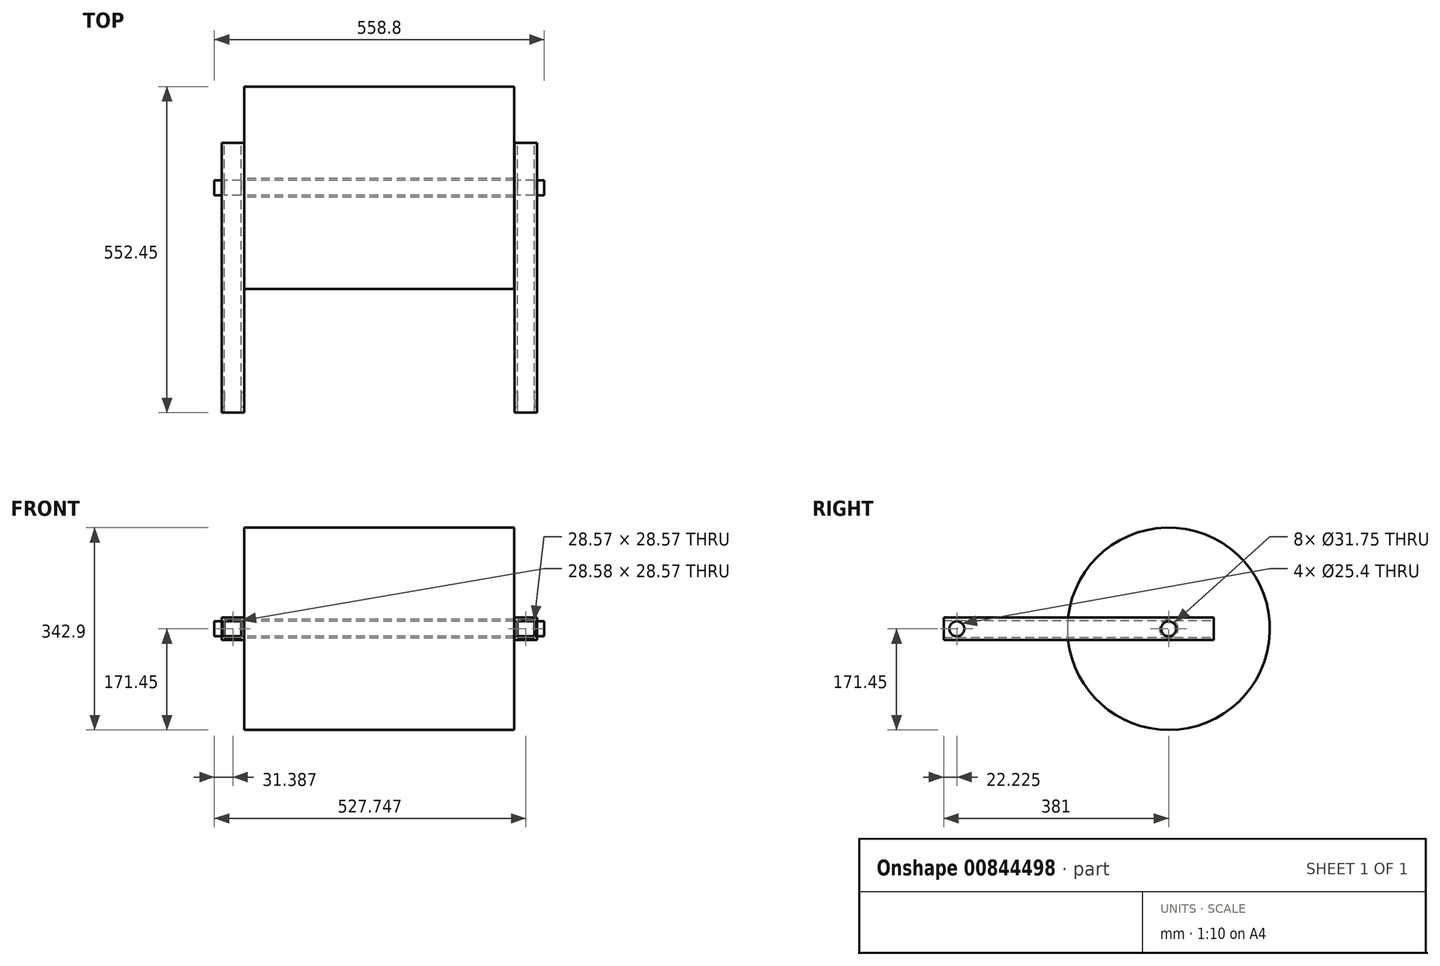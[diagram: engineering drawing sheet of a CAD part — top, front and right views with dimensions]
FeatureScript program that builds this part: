
annotation { "Feature Type Name" : "Feature", "Feature Type Description" : "" }
export const myFeature = defineFeature(function(context is Context, id is Id, definition is map)
    precondition{}
    {
        {
            var Q0;
            Q0=qCreatedBy(makeId("Right.planeOp"),FACE);
            var sketch = newSketch(context, id + "F0", { "sketchPlane" : qUnion([Q0])});
            skCircle(sketch, "E0", {"center": v(0, 0) * mm, "radius": 171.45 * mm});
            skCircle(sketch, "E1", {"center": v(0, 0) * mm, "radius": 15.88 * mm});
            skSolve(sketch);
        }
        {
            var Q0;
            Q0 = qSketchRegion(id + "F0", true);
            extrude(context, id + "F1", {"entities" : qUnion([Q0]), "depth" : 457.2 * mm, "offsetDistance" : 25.4 * mm, "symmetric" : true});
        }
        {
            var Q0;
            Q0=qCreatedBy(makeId("Right.planeOp"),FACE);
            var sketch = newSketch(context, id + "F2", { "sketchPlane" : qUnion([Q0])});
            skCircle(sketch, "E2", {"center": v(0, 0) * mm, "radius": 12.7 * mm});
            skSolve(sketch);
        }
        {
            var Q0;
            Q0 = qSketchRegion(id + "F2", true);
            extrude(context, id + "F3", {"entities" : qUnion([Q0]), "depth" : 558.8 * mm, "offsetDistance" : 25.4 * mm, "symmetric" : true});
        }
        {
            var Q0;
            Q0=qCreatedBy(makeId("Front.planeOp"),FACE);
            var sketch = newSketch(context, id + "F4", { "sketchPlane" : qUnion([Q0])});
            skLineSegment(sketch, "E3.bottom", {"start": v(267.4, -19.05) * mm, "end": v(229.3, -19.05) * mm});
            skLineSegment(sketch, "E3.top", {"start": v(267.4, 19.05) * mm, "end": v(229.3, 19.05) * mm});
            skLineSegment(sketch, "E3.left", {"start": v(267.4, -19.05) * mm, "end": v(267.4, 19.05) * mm});
            skLineSegment(sketch, "E3.right", {"start": v(229.3, -19.05) * mm, "end": v(229.3, 19.05) * mm});
            skPoint(sketch, "E3.middle", {"position": v(248.35, 0) * mm});
            skLineSegment(sketch, "E4.bottom", {"start": v(-228.96, -19.05) * mm, "end": v(-267.06, -19.05) * mm});
            skLineSegment(sketch, "E4.top", {"start": v(-228.96, 19.05) * mm, "end": v(-267.06, 19.05) * mm});
            skLineSegment(sketch, "E4.left", {"start": v(-228.96, -19.05) * mm, "end": v(-228.96, 19.05) * mm});
            skLineSegment(sketch, "E4.right", {"start": v(-267.06, -19.05) * mm, "end": v(-267.06, 19.05) * mm});
            skPoint(sketch, "E4.middle", {"position": v(-248.01, 0) * mm});
            skLineSegment(sketch, "E5.0", {"start": v(262.63, 14.29) * mm, "end": v(234.06, 14.29) * mm});
            skLineSegment(sketch, "E5.1", {"start": v(262.63, -14.29) * mm, "end": v(262.63, 14.29) * mm});
            skLineSegment(sketch, "E5.2", {"start": v(262.63, -14.29) * mm, "end": v(234.06, -14.29) * mm});
            skLineSegment(sketch, "E5.3", {"start": v(234.06, -14.29) * mm, "end": v(234.06, 14.29) * mm});
            skLineSegment(sketch, "E6.0", {"start": v(-233.73, -14.29) * mm, "end": v(-262.3, -14.29) * mm});
            skLineSegment(sketch, "E6.1", {"start": v(-233.73, -14.29) * mm, "end": v(-233.73, 14.29) * mm});
            skLineSegment(sketch, "E6.2", {"start": v(-233.73, 14.29) * mm, "end": v(-262.3, 14.29) * mm});
            skLineSegment(sketch, "E6.3", {"start": v(-262.3, -14.29) * mm, "end": v(-262.3, 14.29) * mm});
            skSolve(sketch);
        }
        {
            var Q0;
            Q0 = qSketchRegion(id + "F4", true);
            extrude(context, id + "F5", {"entities" : qUnion([Q0]), "operationType" : NewBodyOperationType.ADD, "depth" : 381 * mm, "offsetDistance" : 25.4 * mm, "hasSecondDirection" : true, "secondDirectionOppositeDirection" : true, "secondDirectionDepth" : 76.2 * mm});
        }
        {
            var Q0;
            Q0=makeQuery(id+"F5.opExtrude","SWEPT_FACE",FACE,{"disambiguationData":[OSD([sQuery(id+"F4.wireOp",EDGE,"E3.left")])]});
            var sketch = newSketch(context, id + "F6", { "sketchPlane" : qUnion([Q0])});
            skCircle(sketch, "E7", {"center": v(-358.78, 0) * mm, "radius": 12.7 * mm});
            skSolve(sketch);
        }
        {
            var Q0;
            Q0=makeQuery(id+"F6.imprint","IMPRINT",FACE,{"disambiguationData":[TD([[makeQuery(id+"F6.imprint","IMPRINT",EDGE,{"derivedFrom":sQuery(id+"F6.wireOp",EDGE,"E7")}),1.0]])]});
            extrude(context, id + "F7", {"entities" : qUnion([Q0]), "operationType" : NewBodyOperationType.REMOVE, "endBound" : BoundingType.THROUGH_ALL, "oppositeDirection" : true, "depth" : 25.4 * mm, "offsetDistance" : 25.4 * mm});
        }
    });
